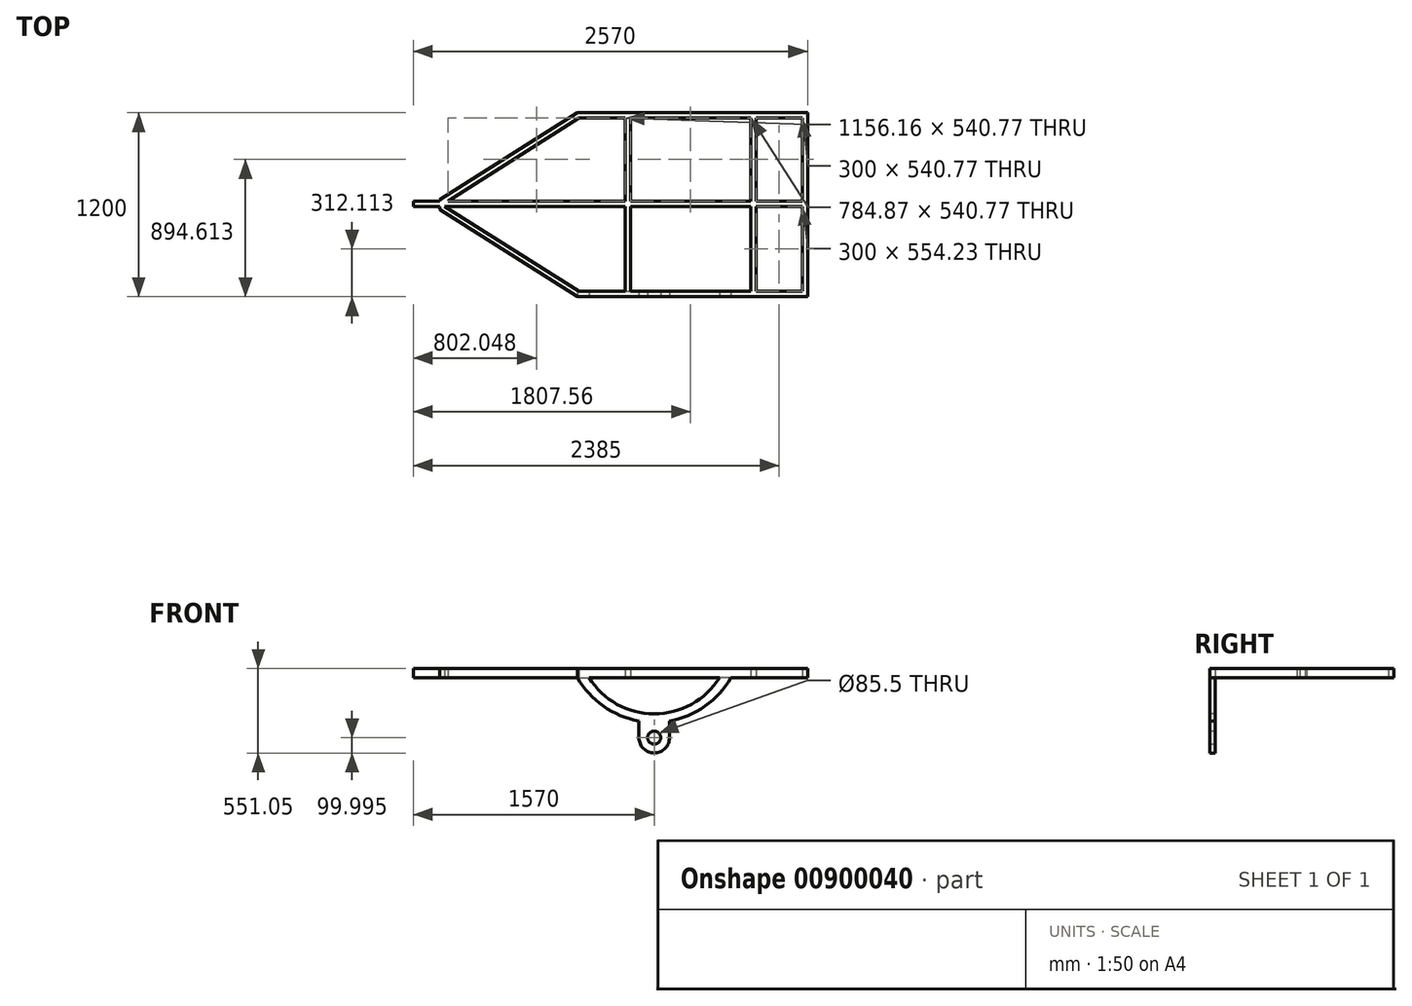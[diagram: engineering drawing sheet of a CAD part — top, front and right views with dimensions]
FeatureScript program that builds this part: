
annotation { "Feature Type Name" : "Feature", "Feature Type Description" : "" }
export const myFeature = defineFeature(function(context is Context, id is Id, definition is map)
    precondition{}
    {
        {
            var Q0;
            Q0=qCreatedBy(makeId("Top.planeOp"),FACE);
            var sketch = newSketch(context, id + "F0", { "sketchPlane" : qUnion([Q0])});
            skLineSegment(sketch, "E0", {"start": v(1186.37, 598.9) * mm, "end": v(1186.37, -601.1) * mm});
            skLineSegment(sketch, "E1", {"start": v(1186.37, -601.1) * mm, "end": v(-313.63, -601.1) * mm});
            skLineSegment(sketch, "E2", {"start": v(-313.63, -601.1) * mm, "end": v(-1213.63, -32.62) * mm});
            skLineSegment(sketch, "E3", {"start": v(-1213.63, -32.62) * mm, "end": v(-1213.63, -11.86) * mm});
            skLineSegment(sketch, "E4", {"start": v(-1213.63, 30.44) * mm, "end": v(-313.63, 598.9) * mm});
            skLineSegment(sketch, "E5", {"start": v(-313.63, 598.9) * mm, "end": v(1186.37, 598.9) * mm});
            skLineSegment(sketch, "E6.1", {"start": v(-303.5, 563.9) * mm, "end": v(-3.5, 563.9) * mm});
            skLineSegment(sketch, "E6.2", {"start": v(1151.37, 563.9) * mm, "end": v(1151.37, 23.14) * mm});
            skLineSegment(sketch, "E6.3", {"start": v(-1159.66, 23.14) * mm, "end": v(-303.5, 563.9) * mm});
            skLineSegment(sketch, "E6.4", {"start": v(1151.37, -566.1) * mm, "end": v(851.37, -566.1) * mm});
            skLineSegment(sketch, "E6.5", {"start": v(-303.5, -566.1) * mm, "end": v(-1180.96, -11.86) * mm});
            skLineSegment(sketch, "E7", {"start": v(851.37, 563.9) * mm, "end": v(851.37, 23.14) * mm});
            skLineSegment(sketch, "E8", {"start": v(816.37, -566.1) * mm, "end": v(816.37, -11.86) * mm});
            skLineSegment(sketch, "E9", {"start": v(-3.5, 563.9) * mm, "end": v(-3.5, 23.14) * mm});
            skLineSegment(sketch, "E10", {"start": v(31.5, -566.1) * mm, "end": v(31.5, -11.86) * mm});
            skLineSegment(sketch, "E11.trimOffspring", {"start": v(31.5, 563.9) * mm, "end": v(816.37, 563.9) * mm});
            skLineSegment(sketch, "E12.trimOffspring", {"start": v(851.37, 563.9) * mm, "end": v(1151.37, 563.9) * mm});
            skLineSegment(sketch, "E13.trimOffspring", {"start": v(-3.5, -566.1) * mm, "end": v(-303.5, -566.1) * mm});
            skLineSegment(sketch, "E14.trimOffspring", {"start": v(816.37, -566.1) * mm, "end": v(31.5, -566.1) * mm});
            skLineSegment(sketch, "E15", {"start": v(-1159.66, 23.14) * mm, "end": v(-3.5, 23.14) * mm});
            skLineSegment(sketch, "E16", {"start": v(1151.37, -11.86) * mm, "end": v(851.37, -11.86) * mm});
            skLineSegment(sketch, "E17", {"start": v(-1213.63, -11.86) * mm, "end": v(-1383.63, -11.86) * mm});
            skLineSegment(sketch, "E18", {"start": v(-1383.63, -11.86) * mm, "end": v(-1383.63, 23.14) * mm});
            skLineSegment(sketch, "E19", {"start": v(-1383.63, 23.14) * mm, "end": v(-1213.63, 23.14) * mm});
            skLineSegment(sketch, "E20.trimOffspring", {"start": v(-1213.63, 23.14) * mm, "end": v(-1213.63, 30.44) * mm});
            skLineSegment(sketch, "E21.trimOffspring", {"start": v(31.5, 23.14) * mm, "end": v(816.37, 23.14) * mm});
            skLineSegment(sketch, "E22.trimOffspring", {"start": v(-3.5, -11.86) * mm, "end": v(-3.5, -566.1) * mm});
            skLineSegment(sketch, "E23.trimOffspring", {"start": v(31.5, 23.14) * mm, "end": v(31.5, 563.9) * mm});
            skLineSegment(sketch, "E24.trimOffspring", {"start": v(-3.5, -11.86) * mm, "end": v(-1180.96, -11.86) * mm});
            skLineSegment(sketch, "E25.trimOffspring", {"start": v(851.37, 23.14) * mm, "end": v(1151.37, 23.14) * mm});
            skLineSegment(sketch, "E26.trimOffspring", {"start": v(816.37, 23.14) * mm, "end": v(816.37, 563.9) * mm});
            skLineSegment(sketch, "E27.trimOffspring", {"start": v(816.37, -11.86) * mm, "end": v(31.5, -11.86) * mm});
            skLineSegment(sketch, "E28.trimOffspring", {"start": v(851.37, -11.86) * mm, "end": v(851.37, -566.1) * mm});
            skLineSegment(sketch, "E29.trimOffspring", {"start": v(1151.37, -11.86) * mm, "end": v(1151.37, -566.1) * mm});
            skSolve(sketch);
        }
        {
            var Q0;
            Q0=makeQuery(id+"F0.imprint","IMPRINT",FACE,{"disambiguationData":[TD([[makeQuery(id+"F0.imprint","IMPRINT",EDGE,{"derivedFrom":sQuery(id+"F0.wireOp",EDGE,"E0")}),-1.0]])]});
            extrude(context, id + "F1", {"entities" : qUnion([Q0]), "depth" : 60 * mm, "offsetDistance" : 25 * mm});
        }
        {
            var Q0;
            Q0=makeQuery(id+"F1.opExtrude","SWEPT_FACE",FACE,{"disambiguationData":[OSD([sQuery(id+"F0.wireOp",EDGE,"E1")])]});
            var sketch = newSketch(context, id + "F2", { "sketchPlane" : qUnion([Q0])});
            skArc(sketch, "E30", {"start": v(-313.63, 0) * mm, "mid": v(-145.18, -185.84) * mm, "end": v(86.37, -282.3) * mm});
            skArc(sketch, "E31", {"start": v(-238.63, 0) * mm, "mid": v(186.37, -236.6) * mm, "end": v(611.37, 0) * mm});
            skArc(sketch, "E32", {"start": v(86.37, -391.05) * mm, "mid": v(186.37, -491.05) * mm, "end": v(286.37, -391.05) * mm});
            skPoint(sketch, "E32.centerSnap0", {"position": v(186.37, -291.05) * mm});
            skLineSegment(sketch, "E33", {"start": v(86.37, -391.05) * mm, "end": v(86.37, -282.3) * mm});
            skLineSegment(sketch, "E34", {"start": v(286.37, -391.05) * mm, "end": v(286.37, -282.3) * mm});
            skArc(sketch, "E35.trimOffspring", {"start": v(286.37, -282.3) * mm, "mid": v(517.91, -185.84) * mm, "end": v(686.37, 0) * mm});
            skCircle(sketch, "E36", {"center": v(186.37, -391.05) * mm, "radius": 42.75 * mm});
            skSolve(sketch);
        }
        {
            var Q0;
            {var subQ4=sQuery(id+"F2.wireOp",EDGE,"E30");Q0=makeQuery(id+"F2.imprint","IMPRINT",FACE,{"disambiguationData":[TD([[makeQuery(id+"F2.imprint","IMPRINT",EDGE,{"derivedFrom":subQ4}),1.0]])]});}
            var Q1;
            Q1=makeQuery(id+"F1.opExtrude","SWEPT_FACE",FACE,{"disambiguationData":[OSD([sQuery(id+"F0.wireOp",EDGE,"E14.trimOffspring")])]});
            extrude(context, id + "F3", {"entities" : qUnion([Q0]), "operationType" : NewBodyOperationType.ADD, "endBound" : BoundingType.UP_TO_SURFACE, "oppositeDirection" : true, "depth" : 60 * mm, "endBoundEntityFace" : qUnion([Q1]), "offsetDistance" : 25 * mm});
        }
    });
